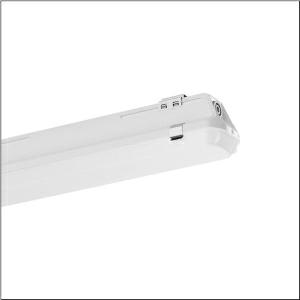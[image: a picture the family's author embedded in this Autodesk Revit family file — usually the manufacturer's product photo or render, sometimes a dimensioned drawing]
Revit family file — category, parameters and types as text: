
# Revit family: monsun_r__21_51fb107l440j005_8a9c
name_source: partatom
category: Lighting Fixtures
units: mm (PartAtom-declared; Revit-internal decimal feet)

## family parameters
Cut with Voids When Loaded = No
Host = Face
Light Source = No
Part Type = Normal
Room Calculation Point = No
Round Connector Dimension = Use Diameter
Shared = No

## types (1)
- Monsun® 21 (1 x LED, 4470 lm, 27.2 W, 4000K)
    Apparent Load = 27 VA
    CIE Flux Codes = 46 76 93 94 100
    Color Rendering = 80
    Color Temperature = 4000K
    Default Elevation = 1800 mm
    Description = Monsun® 21, damp-proof luminaire, chain hanger, primary optical cover: enclosure, of PMMA, light emission: direct distribution, primary light characteristic: symmetric, installation type: suspended mounting, surface-mounted, horizontal mounting, vertical mounting, LED, rated luminous flux: 4.470lm, luminous efficacy: 166lm/W, light colour: 840, colour temperature: 4000K, control gear: ECG, with terminal, 3-pole, max. 2.5mm², through-wiring: 5x 2.5mm², mains connection: 220..240V, AC, 50/60Hz, rated input power: 27W, housing, of glass-fibre reinforced plastic, uncoated, bright grey, incl. chain hanger, length: 1.299mm, width: 90mm, height: 88mm, clip for enclosure, of stainless steel (V2A), ceiling mounting element, of stainless steel (V2A), chain hanger, of stainless steel (V2A), protection rating (complete): IP66, insulation class (complete): insulation class I (protective earthing), certification: CE, ENEC, VDE, UKCA, protection symbol: D, impact resistance: IK04, permissible operating ambient temperature: -25..+35°C, standard: EN 50419, EN 60598-2-1, corresponds to IFS (International Featured Standards) requirements for safety and quality in the food industry, for indoor or canopied outdoor use, no direct snow, no direct sun, no direct rain, contact your sales advisor before using the luminaires in applications with unclear chemical exposure, large temperature fluctuations or condensation-forming humidity, LABS conformity tested according to VDMA 24364:2018-05, packaging unit: 1 piece
    Height = 88 mm
    Lamp = 1 x LED
    Lamp Light Flux = 4470 lm
    Lamp Power = 27.2 W
    Lamp count = 1
    Length = 1299 mm
    Luminous efficacy = 164 lm/W
    Manufacturer = Siteco
    ModVariant = No
    Model = 51FB107L440J005
    Mounting Place = Ceiling
    Mounting Type = Surface mounted
    Number of Poles = 1
    OnlyDefault = Yes
    Power Factor = 1
    Product Name = Monsun® 21
    Product group = damp-proof luminaire
    ProductGroupID = 300
    Protection Class = Protection class I
    Protection Degree = IP 66
    RLX_Detail_Level = 1
    RLX_Emergency_Light_Flux = 0 lm
    RLX_Emergency_Type = 0
    RLX_Emergency_Type_DB = No
    RlxData = <blob elided: 89761 chars, md5=9b4b7ee3>
    Socket = socket
    Standby Power = 0 W
    System Light Flux = 4470 lm
    System Power = 27 W
    Type Comments = Product without accessories
    Type Image = l_1006717.jpg
    URL = http://relux.com
    VarID = ---
    Voltage = 0 V
    Weight = 0.00 kg
    Width = 90 mm

## geometry (parser evidence)
native form markers: Blend x4, Sweep x13
no freeform markers — native parametric forms only
